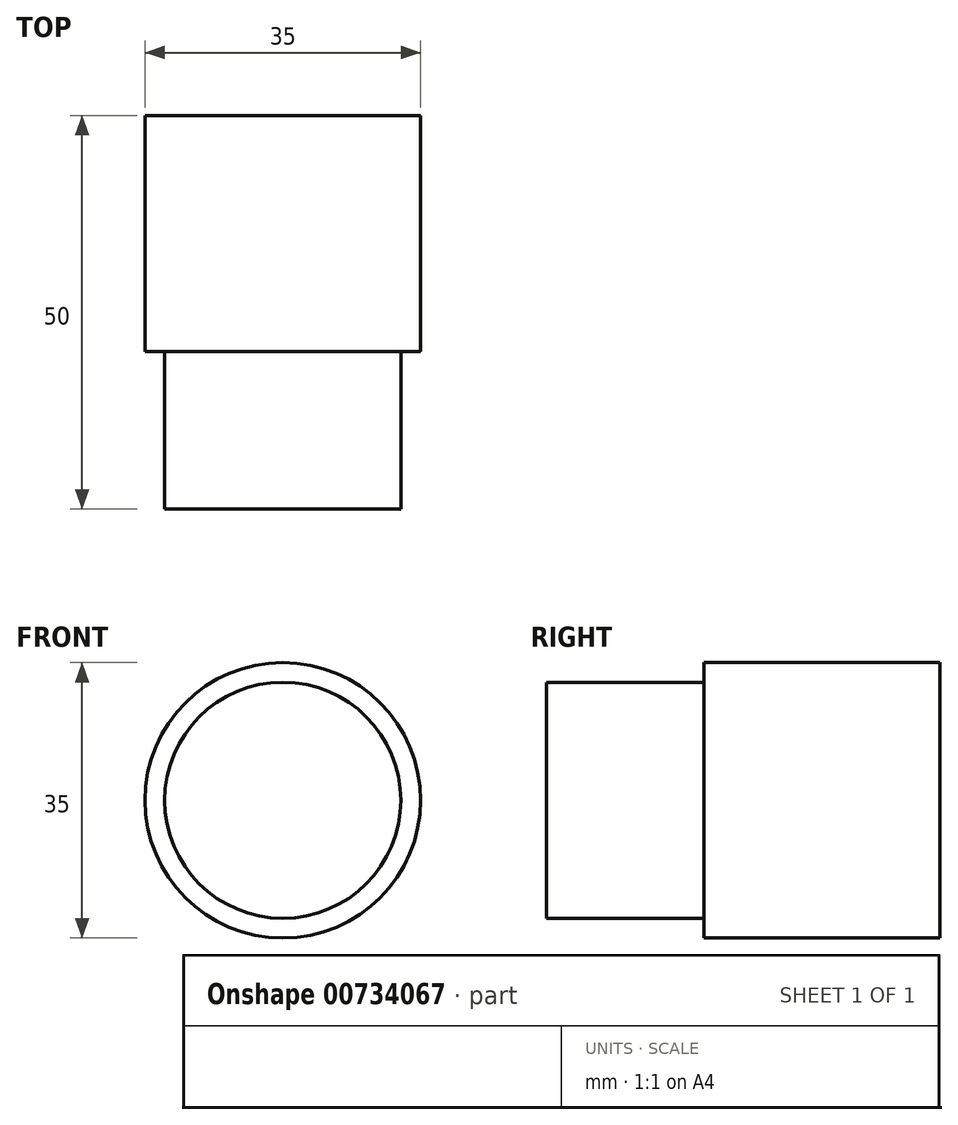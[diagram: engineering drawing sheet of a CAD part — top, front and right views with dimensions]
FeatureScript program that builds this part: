
annotation { "Feature Type Name" : "Feature", "Feature Type Description" : "" }
export const myFeature = defineFeature(function(context is Context, id is Id, definition is map)
    precondition{}
    {
        {
            var Q0;
            Q0=qCreatedBy(makeId("Front.planeOp"),FACE);
            var sketch = newSketch(context, id + "F0", { "sketchPlane" : qUnion([Q0])});
            skCircle(sketch, "E0", {"center": v(0, 0) * mm, "radius": 15 * mm});
            skSolve(sketch);
        }
        {
            var Q0;
            Q0 = qSketchRegion(id + "F0", true);
            extrude(context, id + "F1", {"entities" : qUnion([Q0]), "depth" : 20 * mm, "offsetDistance" : 25.4 * mm});
        }
        {
            var Q0;
            Q0=makeQuery(id+"F1.opExtrude","CAP_FACE",FACE,{"disambiguationData":[OSD([sQuery(id+"F0.wireOp",EDGE,"E0")])],"isStart":true});
            var sketch = newSketch(context, id + "F2", { "sketchPlane" : qUnion([Q0])});
            skCircle(sketch, "E1", {"center": v(0, 0) * mm, "radius": 17.5 * mm});
            skSolve(sketch);
        }
        {
            var Q0;
            Q0 = qSketchRegion(id + "F2", true);
            extrude(context, id + "F3", {"entities" : qUnion([Q0]), "operationType" : NewBodyOperationType.ADD, "depth" : 12.5 * mm, "offsetDistance" : 25.4 * mm});
        }
        {
            var Q0;
            Q0=makeQuery(id+"F3.opExtrude","CAP_FACE",FACE,{"disambiguationData":[OSD([sQuery(id+"F2.wireOp",EDGE,"E1")])],"isStart":false});
            var sketch = newSketch(context, id + "F4", { "sketchPlane" : qUnion([Q0])});
            skCircle(sketch, "E2", {"center": v(0, 0) * mm, "radius": 17.56 * mm});
            skSolve(sketch);
        }
        {
            var Q0;
            Q0=makeQuery(id+"F4.imprint","IMPRINT",FACE,{"disambiguationData":[TD([[makeQuery(id+"F4.imprint","IMPRINT",EDGE,{"derivedFrom":makeQuery(id+"F3.opExtrude","CAP_EDGE",EDGE,{"disambiguationData":[OSD([sQuery(id+"F2.wireOp",EDGE,"E1")])],"isStart":false})}),1.0]])]});
            extrude(context, id + "F5", {"entities" : qUnion([Q0]), "operationType" : NewBodyOperationType.ADD, "depth" : 17.5 * mm, "offsetDistance" : 25.4 * mm});
        }
    });
